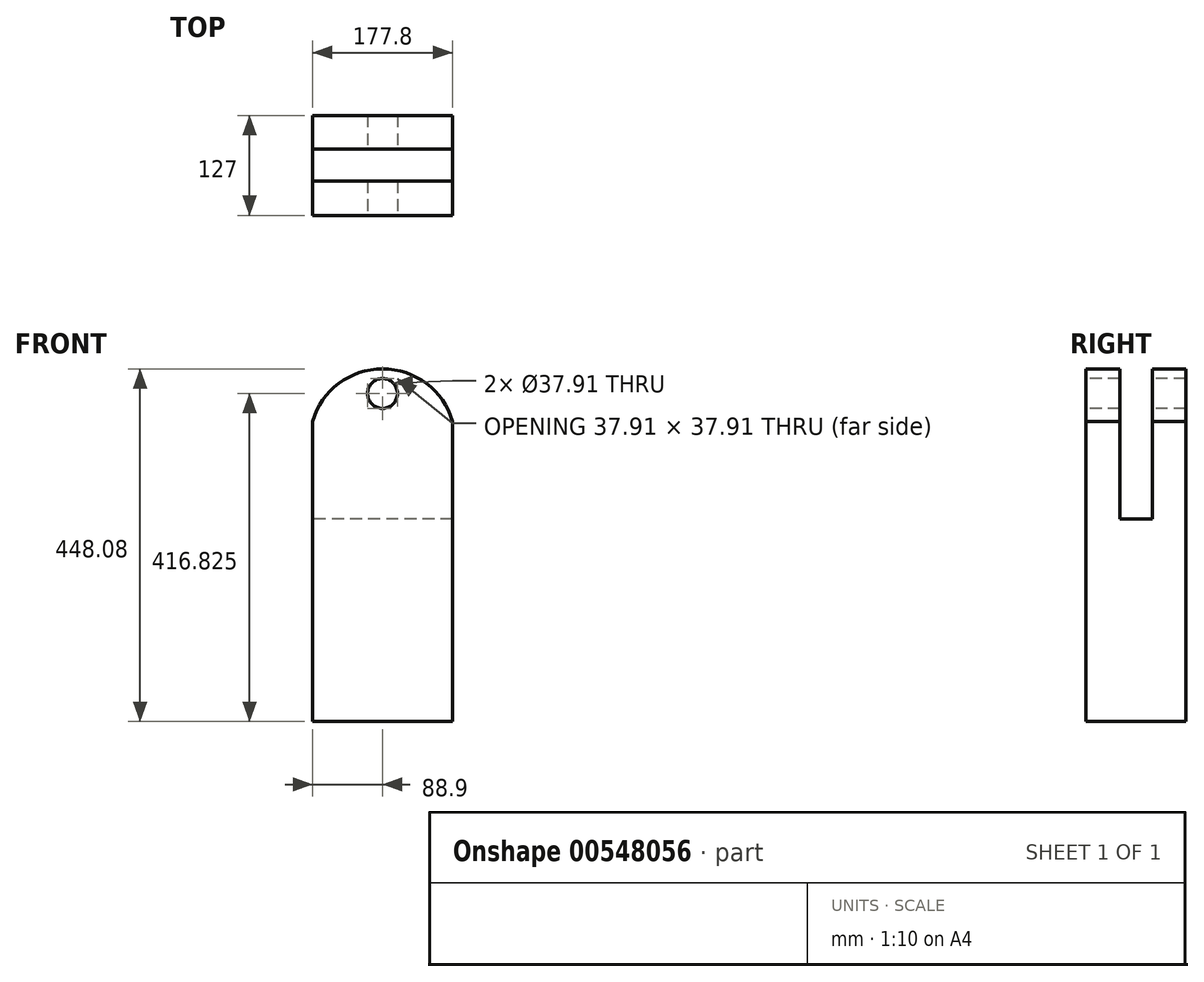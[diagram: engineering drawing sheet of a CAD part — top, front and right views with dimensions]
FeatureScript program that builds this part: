
annotation { "Feature Type Name" : "Feature", "Feature Type Description" : "" }
export const myFeature = defineFeature(function(context is Context, id is Id, definition is map)
    precondition{}
    {
        {
            var Q0;
            Q0=qCreatedBy(makeId("Top.planeOp"),FACE);
            var sketch = newSketch(context, id + "F0", { "sketchPlane" : qUnion([Q0])});
            skLineSegment(sketch, "E0.bottom", {"start": v(-84.26, 62.72) * mm, "end": v(93.54, 62.72) * mm});
            skLineSegment(sketch, "E0.top", {"start": v(-84.26, -64.28) * mm, "end": v(93.54, -64.28) * mm});
            skLineSegment(sketch, "E0.left", {"start": v(-84.26, 62.72) * mm, "end": v(-84.26, -64.28) * mm});
            skLineSegment(sketch, "E0.right", {"start": v(93.54, 62.72) * mm, "end": v(93.54, -64.28) * mm});
            skSolve(sketch);
        }
        {
            var Q0;
            Q0=makeQuery(id+"F0.imprint","IMPRINT",FACE,{"disambiguationData":[TD([[makeQuery(id+"F0.imprint","IMPRINT",EDGE,{"derivedFrom":sQuery(id+"F0.wireOp",EDGE,"E0.bottom")}),-1.0]])]});
            extrude(context, id + "F1", {"entities" : qUnion([Q0]), "depth" : 381 * mm, "offsetDistance" : 25.4 * mm});
        }
        {
            var Q0;
            Q0=makeQuery(id+"F1.opExtrude","SWEPT_FACE",FACE,{"disambiguationData":[OSD([sQuery(id+"F0.wireOp",EDGE,"E0.top")])]});
            var sketch = newSketch(context, id + "F2", { "sketchPlane" : qUnion([Q0])});
            skArc(sketch, "E1", {"start": v(93.54, 381) * mm, "mid": v(4.64, 448.08) * mm, "end": v(-84.26, 381) * mm});
            skLineSegment(sketch, "E2", {"start": v(-84.26, 381) * mm, "end": v(93.54, 381) * mm});
            skCircle(sketch, "E3", {"center": v(4.64, 416.82) * mm, "radius": 18.95 * mm});
            skSolve(sketch);
        }
        {
            var Q0;
            Q0=makeQuery(id+"F2.imprint","IMPRINT",FACE,{"disambiguationData":[TD([[makeQuery(id+"F2.imprint","IMPRINT",EDGE,{"derivedFrom":sQuery(id+"F2.wireOp",EDGE,"E1")}),1.0]])]});
            extrude(context, id + "F3", {"entities" : qUnion([Q0]), "operationType" : NewBodyOperationType.ADD, "oppositeDirection" : true, "depth" : 127 * mm, "offsetDistance" : 25.4 * mm});
        }
        {
            var Q0;
            Q0=makeQuery(id+"F1.opExtrude","SWEPT_FACE",FACE,{"disambiguationData":[OSD([sQuery(id+"F0.wireOp",EDGE,"E0.right")])]});
            var sketch = newSketch(context, id + "F4", { "sketchPlane" : qUnion([Q0])});
            skLineSegment(sketch, "E4.bottom", {"start": v(-20.8, 381) * mm, "end": v(20.11, 381) * mm});
            skLineSegment(sketch, "E4.top", {"start": v(-20.8, 450.38) * mm, "end": v(20.11, 450.38) * mm});
            skLineSegment(sketch, "E4.left", {"start": v(-20.8, 381) * mm, "end": v(-20.8, 450.38) * mm});
            skLineSegment(sketch, "E4.right", {"start": v(20.11, 381) * mm, "end": v(20.11, 450.38) * mm});
            skSolve(sketch);
        }
        {
            var Q0;
            Q0 = qSketchRegion(id + "F4", true);
            extrude(context, id + "F5", {"entities" : qUnion([Q0]), "operationType" : NewBodyOperationType.REMOVE, "oppositeDirection" : true, "depth" : 254 * mm, "offsetDistance" : 25.4 * mm});
        }
        {
            var Q0;
            Q0=makeQuery(id+"F1.opExtrude","SWEPT_FACE",FACE,{"disambiguationData":[OSD([sQuery(id+"F0.wireOp",EDGE,"E0.left")])]});
            var sketch = newSketch(context, id + "F6", { "sketchPlane" : qUnion([Q0])});
            skLineSegment(sketch, "E5.bottom", {"start": v(-20.11, 381) * mm, "end": v(20.8, 381) * mm});
            skLineSegment(sketch, "E5.top", {"start": v(-20.11, 381) * mm, "end": v(20.8, 381) * mm});
            skLineSegment(sketch, "E5.left", {"start": v(-20.11, 381) * mm, "end": v(-20.11, 381) * mm});
            skLineSegment(sketch, "E5.right", {"start": v(20.8, 381) * mm, "end": v(20.8, 381) * mm});
            skLineSegment(sketch, "E6.bottom", {"start": v(20.8, 381) * mm, "end": v(-20.11, 381) * mm});
            skLineSegment(sketch, "E6.top", {"start": v(20.8, 257.64) * mm, "end": v(-20.11, 257.64) * mm});
            skLineSegment(sketch, "E6.left", {"start": v(20.8, 381) * mm, "end": v(20.8, 257.64) * mm});
            skLineSegment(sketch, "E6.right", {"start": v(-20.11, 381) * mm, "end": v(-20.11, 257.64) * mm});
            skSolve(sketch);
        }
        {
            var Q0;
            Q0 = qSketchRegion(id + "F6", true);
            extrude(context, id + "F7", {"entities" : qUnion([Q0]), "operationType" : NewBodyOperationType.REMOVE, "oppositeDirection" : true, "depth" : 254 * mm, "offsetDistance" : 25.4 * mm});
        }
    });
